# Revit family: Electronics_Commercial-Loudspeakers-Back-Can_Biamp_Full-Range_CM10TB
name_source: partatom
category: Communication Devices
units: mm (PartAtom-declared; Revit-internal decimal feet)

## family parameters
Cut with Voids When Loaded = No
Host = Face
Maintain Annotation Orientation = No
OmniClass Number = 23.85.10.11.14.14.14
OmniClass Title = Loudspeakers
Part Type = Normal
Room Calculation Point = No
Round Connector Dimension = Use Diameter
Shared = No

## types (1)
- CM10TB
    Compliance = ETL listed to comply with UL1480, UL2043 and CSA62368-1 Suitable for use in air handling spaces per NFPA 70 and NFPA 90
    Connector Description = Terminal block; 9 V (10 W @ 8 Ω),70/100V operation
    Controls = Wattage / low impedance selector switch
    Default Elevation = 48 "
    Depth = 9 "
    Description = CM10TB Full-Range 5.5-Inch 2 FT X 2 FT Ceiling Mount Loudspeaker
    Diameter = 6 "
    Grill Material = Biamp - Plastic - White(Grid)
    Housing Material = Biamp - Metal - White
    Input Connection = 4-position terminal block
    Manufacturer = Biamp
    Model = CM10TB
    Mounting Provisions = 2 mounting clamps with 46 mm (1.8) grip range
    Nominal Beamwidth (H x V) = 145°, (conical)
    Nominal Continuous Power Handling = Passive 9 V (10 W @ 8 Ω)
    Nominal Maximum SPL(Processed) = Peak - 109dB; Continuous - 103dB
    Operating Environment = Indoor
    Operating Mode = Passive with selectable low-impedance or 70 V/100 V operation
    Operating Range (-10dB) = 120 Hz to 20 kHz
    Product Documentation Link = https://downloads.biamp.com
    Product Page URL = https://www.biamp.com
    Product data url = https://bimobject.com
    Rated Continuous Voltage = 9 V (19 dBV)
    Rated Maximum SPL(Processed) = Peak - 115dB; Continuous - 103dB
    Recommended Amplifers = 10 W - 20 W, 8 Ω (9 V - 13 V)
    Required Accessories = 130 Hz, 12 dB / oct. Butterworth high pass flter;DSP presets for Tesira or ALCs
    Sensitivity = 1 m; 94 dB (2.83 V) ;94 dB (1 W, 8 Ω)
    Transducer = Full-range 1 x 5.5 (140 mm) paper diaphragm driver
    Transformer = 70 V: 10 W, 5 W, 2.5 W, 1.25 W, 0.625 W;  100 V: 10 W, 5 W, 2.5 W, 1.25 W
    URL = https://www.biamp.com
    Version = 1
    Weight = 4.60 lb

## geometry (parser evidence)
native form markers: Sweep x6
no freeform markers — native parametric forms only
